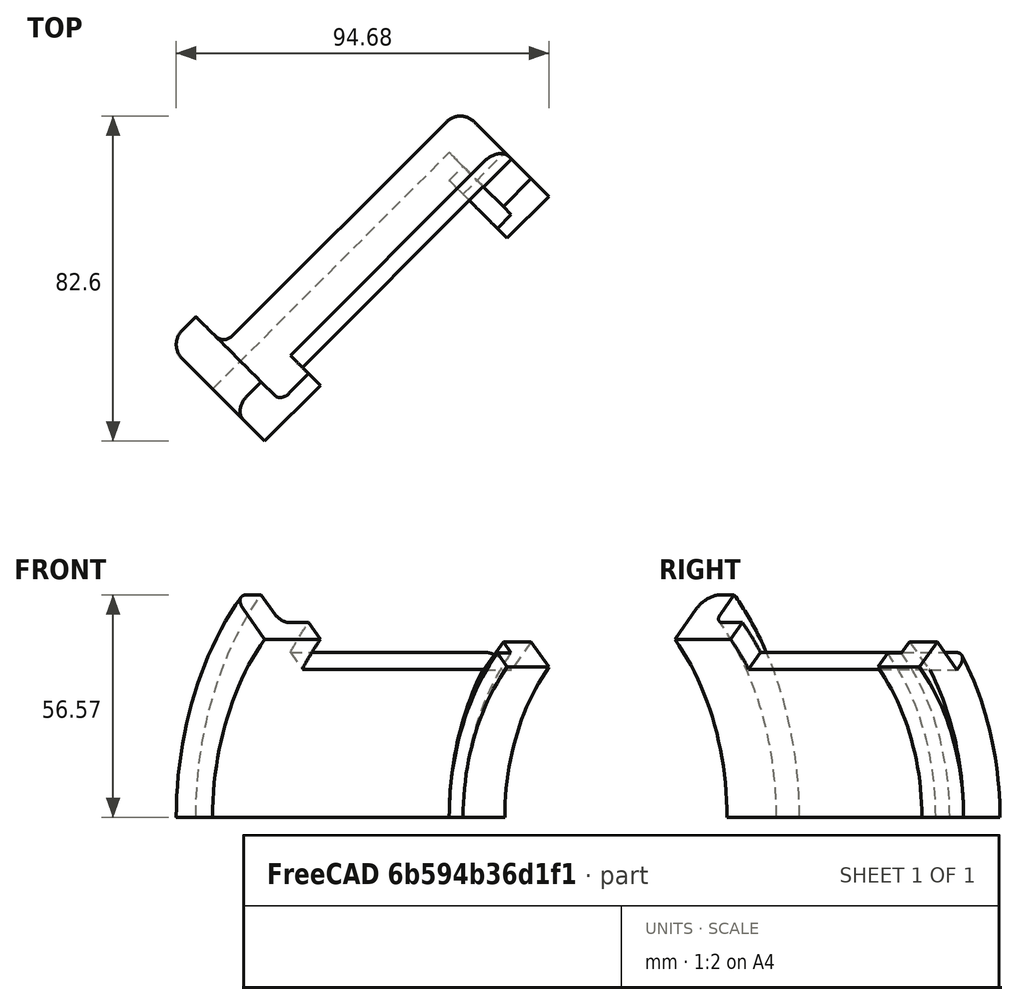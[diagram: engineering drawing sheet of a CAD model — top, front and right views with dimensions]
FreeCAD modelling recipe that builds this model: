
FCSTD DOCUMENT  (FreeCAD 0.15R4671 (Git))
Label: sphere_support_cyls4_w3
License: All rights reserved
LicenseURL: http://en.wikipedia.org/wiki/All_rights_reserved
objects: Part::Cut×11, Part::Box×8, Part::Cylinder×6, Part::Fillet×3, Part::MultiFuse×2
note: 30 computed .brp shape members not serialized (recipe doc carries the construction recipe); baked Part::Feature solids carry a one-line shape summary decoded from their .brp

FEATURE [Part::Cylinder] Cylinder  label="Base_Cylinder"
  Angle = 360
  Height = 10
  Radius = 80
FEATURE [Part::Cylinder] Cylinder001  label="Body_Cylinder"
  Angle = 360
  Height = 90
  Placement = pos=(0,0,5) rot=(0,0,1;0rad)
  Radius = 70
FEATURE [Part::MultiFuse] Fusion  label="Core_Fusion"
  Shapes = -> [Cylinder,Cylinder001]
FEATURE [Part::Cylinder] Cylinder002  label="Inner_Hole"
  Angle = 360
  Height = 85
  Radius = 64
FEATURE [Part::Cut] Cut
  Base = -> Fusion
  Tool = -> Cylinder002
FEATURE [Part::Cylinder] Cylinder003  label="Inner_Lip"
  Angle = 360
  Height = 10
  Placement = pos=(0,0,80) rot=(0,0,1;0rad)
  Radius = 59
FEATURE [Part::MultiFuse] Fusion001
  Shapes = -> [Cut,Cylinder003]
FEATURE [Part::Cylinder] Cylinder004  label="Through_Hole"
  Angle = 360
  Height = 100
  Radius = 54
FEATURE [Part::Cut] Cut001
  Base = -> Fusion001
  Tool = -> Cylinder004
FEATURE [Part::Fillet] Fillet
  Base = -> Cut001
  Edges = 1 edges r=3: [Edge12]
FEATURE [Part::Fillet] Fillet001
  Base = -> Fillet
  Edges = 1 edges r=5: [Edge11]
FEATURE [Part::Fillet] Fillet002
  Base = -> Fillet001
  Edges = 1 edges r=5: [Edge13]
FEATURE [Part::Cylinder] Cylinder005  label="Bearing_Holes"
  Angle = 360
  Height = 180
  Placement = pos=(0,90,65) rot=(1,0,0;1.5708rad)
  Radius = 10
FEATURE [Part::Cut] Cut002
  Base = -> Fillet002
  Tool = -> Cylinder005
FEATURE [Part::Box] Box  label="Bearing_Slot"
  Height = 35
  Length = 20
  Placement = pos=(-10,48,65) rot=(0,0,1;0rad)
  Width = 25
FEATURE [Part::Cut] Cut003
  Base = -> Cut002
  Tool = -> Box
FEATURE [Part::Box] Box001  label="Cube"
  Height = 35
  Length = 10
  Placement = pos=(0,48,65) rot=(0,1,0;0.261799rad)
  Width = 25
FEATURE [Part::Cut] Cut004
  Base = -> Cut003
  Tool = -> Box001
FEATURE [Part::Box] Box002  label="Cube001"
  Height = 35
  Length = 10
  Placement = pos=(-9.95,48,64) rot=(0,-1,0;0.261799rad)
  Width = 25
FEATURE [Part::Cut] Cut005
  Base = -> Cut004
  Tool = -> Box002
FEATURE [Part::Box] Box003  label="Tab_Cut_R"
  Height = 80
  Length = 20
  Placement = pos=(63,-10,20) rot=(0,0,1;0rad)
  Width = 20
FEATURE [Part::Cut] Cut006
  Base = -> Cut005
  Tool = -> Box003
FEATURE [Part::Box] Box004  label="Tab_Cut_L"
  Height = 80
  Length = 20
  Placement = pos=(-83,-10,20) rot=(0,0,1;0rad)
  Width = 20
FEATURE [Part::Cut] Cut007
  Base = -> Cut006
  Tool = -> Box004
FEATURE [Part::Box] Box005  label="Cube002"
  Height = 100
  Length = 100
  Placement = pos=(0,0,0) rot=(0,0,1;3.14159rad)
  Width = 100
FEATURE [Part::Cut] Cut008
  Base = -> Cut007
  Tool = -> Box005
FEATURE [Part::Box] Box006  label="Cube003"
  Height = 100
  Length = 100
  Placement = pos=(71,-71,0) rot=(0,0,1;0.785398rad)
  Width = 200
FEATURE [Part::Cut] Cut009
  Base = -> Cut008
  Placement = pos=(0,0,0) rot=(-0.707107,0.707107,0;1.5708rad)
  Tool = -> Box006
FEATURE [Part::Box] Box007  label="Cube004"
  Height = 100
  Length = 100
  Placement = pos=(0,0,0) rot=(0,0,-1;0.785398rad)
  Width = 100
FEATURE [Part::Cut] Cut010
  Base = -> Cut009
  Tool = -> Box007
